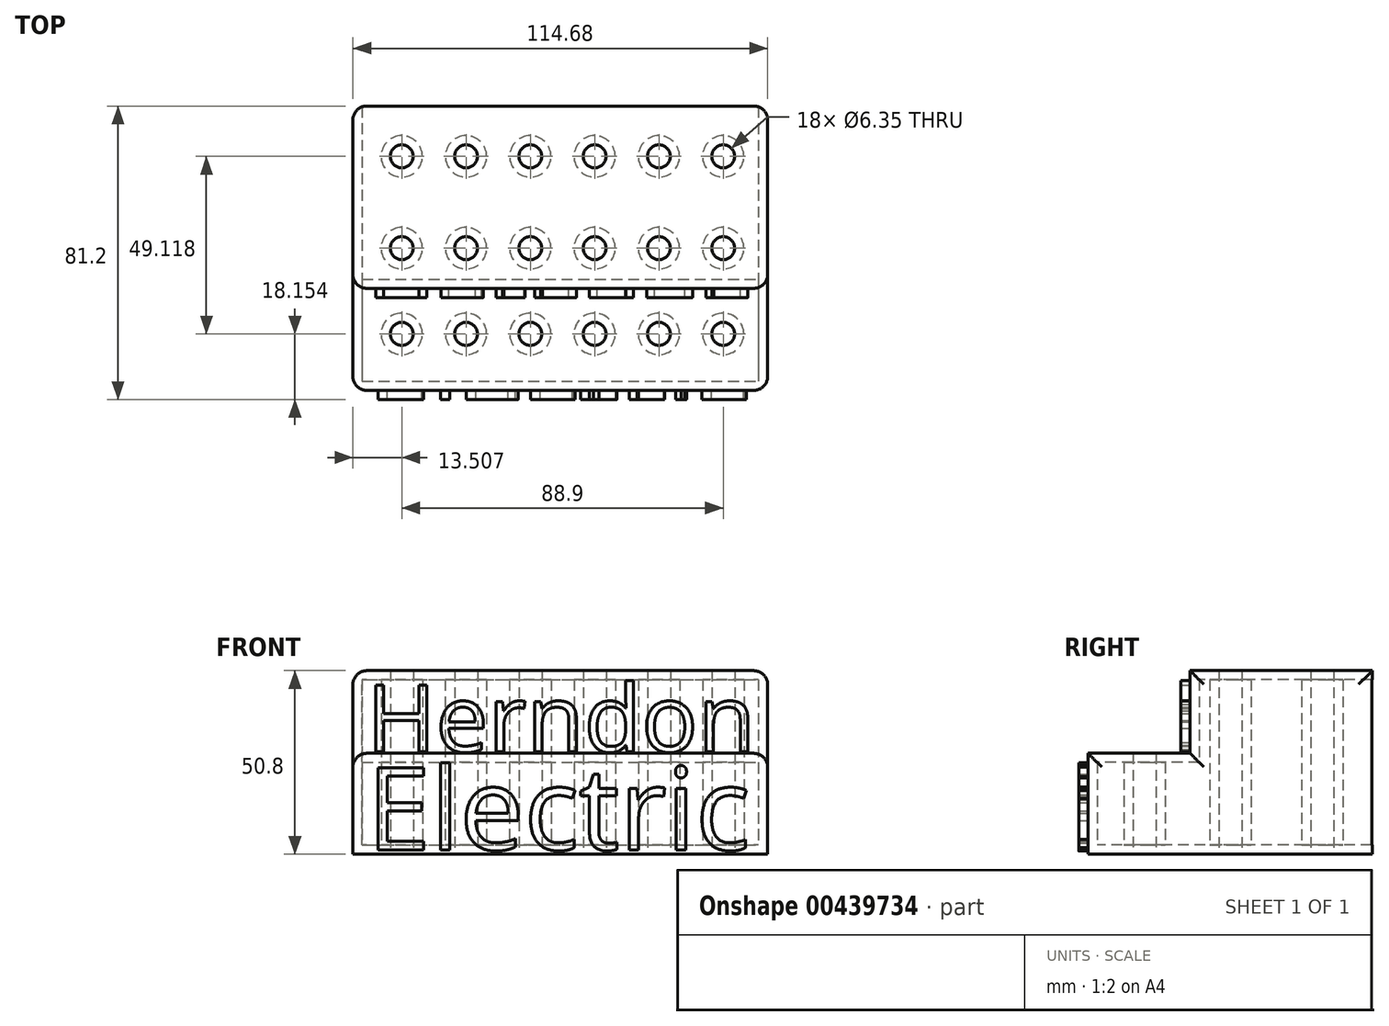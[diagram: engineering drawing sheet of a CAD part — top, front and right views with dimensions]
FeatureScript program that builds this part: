
annotation { "Feature Type Name" : "Feature", "Feature Type Description" : "" }
export const myFeature = defineFeature(function(context is Context, id is Id, definition is map)
    precondition{}
    {
        {
            var Q0;
            Q0=qCreatedBy(makeId("Top.planeOp"),FACE);
            var sketch = newSketch(context, id + "F0", { "sketchPlane" : qUnion([Q0])});
            skLineSegment(sketch, "E0.bottom", {"start": v(-44.73, 28.97) * mm, "end": v(69.95, 28.97) * mm});
            skLineSegment(sketch, "E0.top", {"start": v(-44.73, -21.47) * mm, "end": v(69.95, -21.47) * mm});
            skLineSegment(sketch, "E0.left", {"start": v(-44.73, 28.97) * mm, "end": v(-44.73, -21.47) * mm});
            skLineSegment(sketch, "E0.right", {"start": v(69.95, 28.97) * mm, "end": v(69.95, -21.47) * mm});
            skLineSegment(sketch, "E1.top", {"start": v(-44.73, -49.69) * mm, "end": v(69.95, -49.69) * mm});
            skLineSegment(sketch, "E1.left", {"start": v(-44.73, -21.47) * mm, "end": v(-44.73, -49.69) * mm});
            skLineSegment(sketch, "E1.right", {"start": v(69.95, -21.47) * mm, "end": v(69.95, -49.69) * mm});
            skPoint(sketch, "E2", {"position": v(-31.22, -10.36) * mm});
            skPoint(sketch, "E3.0.1.0", {"position": v(-31.22, 15.04) * mm});
            skPoint(sketch, "E3.1.0.0", {"position": v(-13.44, -10.36) * mm});
            skPoint(sketch, "E3.1.1.0", {"position": v(-13.44, 15.04) * mm});
            skPoint(sketch, "E3.2.0.0", {"position": v(4.34, -10.36) * mm});
            skPoint(sketch, "E3.2.1.0", {"position": v(4.34, 15.04) * mm});
            skPoint(sketch, "E3.3.0.0", {"position": v(22.12, -10.36) * mm});
            skPoint(sketch, "E3.3.1.0", {"position": v(22.12, 15.04) * mm});
            skPoint(sketch, "E3.4.0.0", {"position": v(39.9, -10.36) * mm});
            skPoint(sketch, "E3.4.1.0", {"position": v(39.9, 15.04) * mm});
            skPoint(sketch, "E3.5.0.0", {"position": v(57.68, -10.36) * mm});
            skPoint(sketch, "E3.5.1.0", {"position": v(57.68, 15.04) * mm});
            skLineSegment(sketch, "E3.direction1", {"start": v(-31.22, -10.36) * mm, "end": v(-13.44, -10.36) * mm, "construction": true});
            skLineSegment(sketch, "E3.direction2", {"start": v(-31.22, -10.36) * mm, "end": v(-31.22, 15.04) * mm, "construction": true});
            skPoint(sketch, "E4", {"position": v(-31.22, -34.08) * mm});
            skPoint(sketch, "E5.1.0.0", {"position": v(-13.44, -34.08) * mm});
            skPoint(sketch, "E5.2.0.0", {"position": v(4.34, -34.08) * mm});
            skPoint(sketch, "E5.3.0.0", {"position": v(22.12, -34.08) * mm});
            skPoint(sketch, "E5.4.0.0", {"position": v(39.9, -34.08) * mm});
            skPoint(sketch, "E5.5.0.0", {"position": v(57.68, -34.08) * mm});
            skLineSegment(sketch, "E5.direction1", {"start": v(-31.22, -34.08) * mm, "end": v(-13.44, -34.08) * mm, "construction": true});
            skSolve(sketch);
        }
        {
            var Q0;
            Q0=makeQuery(id+"F0.imprint","IMPRINT",FACE,{"disambiguationData":[TD([[makeQuery(id+"F0.imprint","IMPRINT",EDGE,{"derivedFrom":sQuery(id+"F0.wireOp",EDGE,"E0.bottom")}),-1.0]])]});
            extrude(context, id + "F1", {"entities" : qUnion([Q0]), "depth" : 50.8 * mm});
        }
        {
            var Q0;
            Q0=makeQuery(id+"F0.imprint","IMPRINT",FACE,{"disambiguationData":[TD([[makeQuery(id+"F0.imprint","IMPRINT",EDGE,{"derivedFrom":sQuery(id+"F0.wireOp",EDGE,"E0.top")}),-1.0]])]});
            extrude(context, id + "F2", {"entities" : qUnion([Q0]), "operationType" : NewBodyOperationType.ADD, "depth" : 27.94 * mm});
        }
        {
            var Q0;
            Q0=sQuery(id+"F0.wireOp",VERTEX,"E3.0.1.0");
            var Q1;
            Q1=sQuery(id+"F0.wireOp",VERTEX,"E3.1.1.0");
            var Q2;
            Q2=sQuery(id+"F0.wireOp",VERTEX,"E3.2.1.0");
            var Q3;
            Q3=sQuery(id+"F0.wireOp",VERTEX,"E3.3.1.0");
            var Q4;
            Q4=sQuery(id+"F0.wireOp",VERTEX,"E3.4.1.0");
            var Q5;
            Q5=sQuery(id+"F0.wireOp",VERTEX,"E3.5.1.0");
            var Q6;
            Q6=sQuery(id+"F0.wireOp",VERTEX,"E3.5.0.0");
            var Q7;
            Q7=sQuery(id+"F0.wireOp",VERTEX,"E5.5.0.0");
            var Q8;
            Q8=sQuery(id+"F0.wireOp",VERTEX,"E5.4.0.0");
            var Q9;
            Q9=sQuery(id+"F0.wireOp",VERTEX,"E5.3.0.0");
            var Q10;
            Q10=sQuery(id+"F0.wireOp",VERTEX,"E5.2.0.0");
            var Q11;
            Q11=sQuery(id+"F0.wireOp",VERTEX,"E5.1.0.0");
            var Q12;
            Q12=sQuery(id+"F0.wireOp",VERTEX,"E4");
            var Q13;
            Q13=sQuery(id+"F0.wireOp",VERTEX,"E2");
            var Q14;
            Q14=sQuery(id+"F0.wireOp",VERTEX,"E3.1.0.0");
            var Q15;
            Q15=sQuery(id+"F0.wireOp",VERTEX,"E3.2.0.0");
            var Q16;
            Q16=sQuery(id+"F0.wireOp",VERTEX,"E3.3.0.0");
            var Q17;
            Q17=sQuery(id+"F0.wireOp",VERTEX,"E3.4.0.0");
            var Q18;
            Q18=makeQuery(id+"F1.opExtrude","SWEPT_BODY",BODY,{"disambiguationData":[OSD([sQuery(id+"F0.wireOp",EDGE,"E0.bottom"),sQuery(id+"F0.wireOp",EDGE,"E0.left"),sQuery(id+"F0.wireOp",EDGE,"E0.right"),sQuery(id+"F0.wireOp",EDGE,"E0.top")])]});
            hole(context, id + "F3", {"style" : HoleStyle.SIMPLE, "endStyle" : HoleEndStyle.THROUGH, "oppositeDirection" : true, "holeDiameter" : 6.35 * mm, "isTappedThrough" : true, "tappedDepth" : 12.7 * mm, "tapClearance" : 3, "locations" : qUnion([Q0, Q1, Q2, Q3, Q4, Q5, Q6, Q7, Q8, Q9, Q10, Q11, Q12, Q13, Q14, Q15, Q16, Q17]), "scope" : qUnion([Q18])});
        }
        {
            var Q0;
            Q0=makeQuery(id+"F1.opExtrude","SWEPT_FACE",FACE,{"disambiguationData":[OSD([sQuery(id+"F0.wireOp",EDGE,"E0.bottom")])]});
            shell(context, id + "F4", {"entities" : qUnion([Q0]), "thickness" : 2.54 * mm});
        }
        {
            var Q0;
            Q0=makeQuery(id+"F2.opExtrude","CAP_EDGE",EDGE,{"disambiguationData":[OSD([sQuery(id+"F0.wireOp",EDGE,"E1.right")])],"isStart":false});
            var Q1;
            Q1=makeQuery(id+"F1.opExtrude","CAP_EDGE",EDGE,{"disambiguationData":[OSD([sQuery(id+"F0.wireOp",EDGE,"E0.right")])],"isStart":false});
            var Q2;
            Q2=makeQuery(id+"F1.opExtrude","SWEPT_EDGE",EDGE,{"disambiguationData":[OSD([sQuery(id+"F0.wireOp",EDGE,"E0.right"),sQuery(id+"F0.wireOp",EDGE,"E0.top"),sQuery(id+"F0.wireOp",EDGE,"E1.right")])]});
            var Q3;
            Q3=makeQuery(id+"F2.opExtrude","SWEPT_EDGE",EDGE,{"disambiguationData":[OSD([sQuery(id+"F0.wireOp",EDGE,"E1.top"),sQuery(id+"F0.wireOp",EDGE,"E1.right")])]});
            var Q4;
            Q4=makeQuery(id+"F1.opExtrude","SWEPT_EDGE",EDGE,{"disambiguationData":[OSD([sQuery(id+"F0.wireOp",EDGE,"E0.bottom"),sQuery(id+"F0.wireOp",EDGE,"E0.right")])]});
            var Q5;
            Q5=makeQuery(id+"F1.opExtrude","SWEPT_EDGE",EDGE,{"disambiguationData":[OSD([sQuery(id+"F0.wireOp",EDGE,"E0.bottom"),sQuery(id+"F0.wireOp",EDGE,"E0.left")])]});
            var Q6;
            Q6=makeQuery(id+"F1.opExtrude","CAP_EDGE",EDGE,{"disambiguationData":[OSD([sQuery(id+"F0.wireOp",EDGE,"E0.left")])],"isStart":false});
            var Q7;
            Q7=makeQuery(id+"F1.opExtrude","SWEPT_EDGE",EDGE,{"disambiguationData":[OSD([sQuery(id+"F0.wireOp",EDGE,"E0.left"),sQuery(id+"F0.wireOp",EDGE,"E0.top"),sQuery(id+"F0.wireOp",EDGE,"E1.left")])]});
            var Q8;
            Q8=makeQuery(id+"F2.opExtrude","CAP_EDGE",EDGE,{"disambiguationData":[OSD([sQuery(id+"F0.wireOp",EDGE,"E1.left")])],"isStart":false});
            var Q9;
            Q9=makeQuery(id+"F2.opExtrude","SWEPT_EDGE",EDGE,{"disambiguationData":[OSD([sQuery(id+"F0.wireOp",EDGE,"E1.top"),sQuery(id+"F0.wireOp",EDGE,"E1.left")])]});
            fillet(context, id + "F5", {"entities" : qUnion([Q0, Q1, Q2, Q3, Q4, Q5, Q6, Q7, Q8, Q9]), "radius" : 3.8 * mm, "tangentPropagation" : true, "allowEdgeOverflow" : false});
        }
        {
            var Q0;
            Q0=makeQuery(id+"F1.opExtrude","SWEPT_FACE",FACE,{"disambiguationData":[OSD([sQuery(id+"F0.wireOp",EDGE,"E0.top")])]});
            var sketch = newSketch(context, id + "F6", { "sketchPlane" : qUnion([Q0])});
            skText(sketch, "E6", { "text": "Herndon", "fontName": "OpenSans-Regular.ttf"});
            const initialGuessF6  = {"E6": [-0.04092, 0.02835, 1, 0, 0.01864]};
            skSetInitialGuess(sketch, initialGuessF6);
            skSolve(sketch);
        }
        {
            var Q0;
            Q0=makeQuery(id+"F2.opExtrude","SWEPT_FACE",FACE,{"disambiguationData":[OSD([sQuery(id+"F0.wireOp",EDGE,"E1.top")])]});
            var sketch = newSketch(context, id + "F7", { "sketchPlane" : qUnion([Q0])});
            skText(sketch, "E7", { "text": "Electric\n", "fontName": "OpenSans-Regular.ttf"});
            const initialGuessF7  = {"E7": [-0.04092, 0.00124, 1, 0, 0.02289]};
            skSetInitialGuess(sketch, initialGuessF7);
            skSolve(sketch);
        }
        {
            var Q0;
            Q0 = qSketchRegion(id + "F6", true);
            var Q1;
            Q1 = qSketchRegion(id + "F7", true);
            extrude(context, id + "F8", {"entities" : qUnion([Q0, Q1]), "operationType" : NewBodyOperationType.ADD, "depth" : 2.54 * mm});
        }
    });
